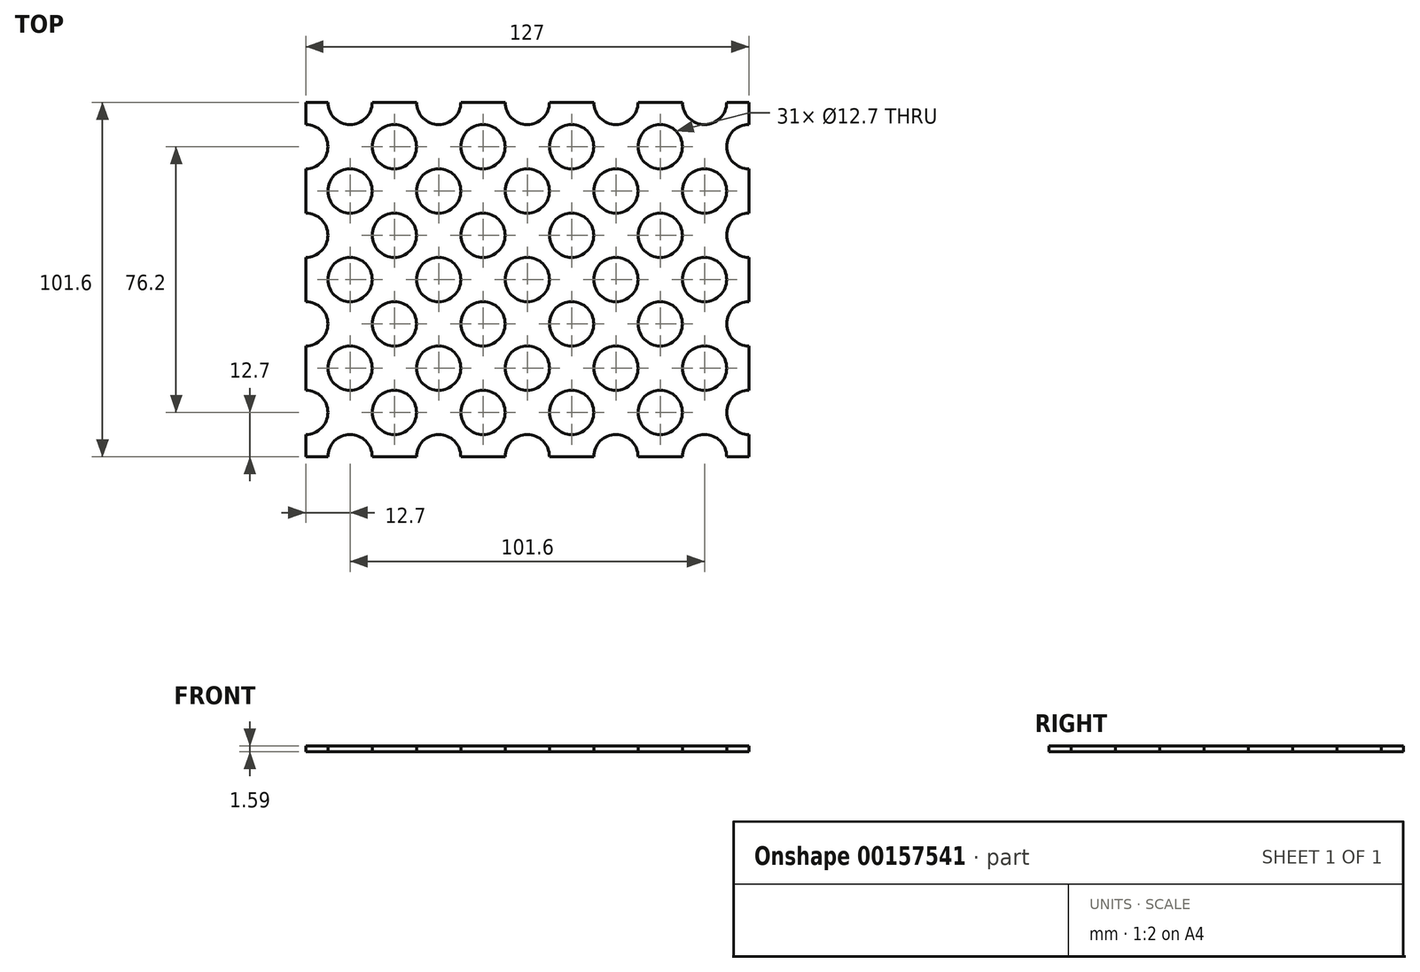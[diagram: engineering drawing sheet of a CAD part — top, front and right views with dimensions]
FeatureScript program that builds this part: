
annotation { "Feature Type Name" : "Feature", "Feature Type Description" : "" }
export const myFeature = defineFeature(function(context is Context, id is Id, definition is map)
    precondition{}
    {
        {
            var Q0;
            Q0=qCreatedBy(makeId("Top.planeOp"),FACE);
            var sketch = newSketch(context, id + "F0", { "sketchPlane" : qUnion([Q0])});
            skLineSegment(sketch, "E0.bottom", {"start": v(-63.5, -50.8) * mm, "end": v(63.5, -50.8) * mm});
            skLineSegment(sketch, "E0.top", {"start": v(-63.5, 50.8) * mm, "end": v(63.5, 50.8) * mm});
            skLineSegment(sketch, "E0.left", {"start": v(-63.5, -50.8) * mm, "end": v(-63.5, 50.8) * mm});
            skLineSegment(sketch, "E0.right", {"start": v(63.5, -50.8) * mm, "end": v(63.5, 50.8) * mm});
            skCircle(sketch, "E1", {"center": v(-63.5, 38.1) * mm, "radius": 6.35 * mm});
            skCircle(sketch, "E2.0.1.0", {"center": v(-63.5, 12.7) * mm, "radius": 6.35 * mm});
            skCircle(sketch, "E2.0.2.0", {"center": v(-63.5, -12.7) * mm, "radius": 6.35 * mm});
            skCircle(sketch, "E2.1.0.0", {"center": v(-38.1, 38.1) * mm, "radius": 6.35 * mm});
            skCircle(sketch, "E2.1.1.0", {"center": v(-38.1, 12.7) * mm, "radius": 6.35 * mm});
            skCircle(sketch, "E2.1.2.0", {"center": v(-38.1, -12.7) * mm, "radius": 6.35 * mm});
            skCircle(sketch, "E2.2.0.0", {"center": v(-12.7, 38.1) * mm, "radius": 6.35 * mm});
            skCircle(sketch, "E2.2.1.0", {"center": v(-12.7, 12.7) * mm, "radius": 6.35 * mm});
            skCircle(sketch, "E2.2.2.0", {"center": v(-12.7, -12.7) * mm, "radius": 6.35 * mm});
            skCircle(sketch, "E2.3.0.0", {"center": v(12.7, 38.1) * mm, "radius": 6.35 * mm});
            skCircle(sketch, "E2.3.1.0", {"center": v(12.7, 12.7) * mm, "radius": 6.35 * mm});
            skCircle(sketch, "E2.3.2.0", {"center": v(12.7, -12.7) * mm, "radius": 6.35 * mm});
            skCircle(sketch, "E2.4.0.0", {"center": v(38.1, 38.1) * mm, "radius": 6.35 * mm});
            skCircle(sketch, "E2.4.1.0", {"center": v(38.1, 12.7) * mm, "radius": 6.35 * mm});
            skCircle(sketch, "E2.4.2.0", {"center": v(38.1, -12.7) * mm, "radius": 6.35 * mm});
            skCircle(sketch, "E2.5.0.0", {"center": v(63.5, 38.1) * mm, "radius": 6.35 * mm});
            skCircle(sketch, "E2.5.1.0", {"center": v(63.5, 12.7) * mm, "radius": 6.35 * mm});
            skCircle(sketch, "E2.5.2.0", {"center": v(63.5, -12.7) * mm, "radius": 6.35 * mm});
            skLineSegment(sketch, "E2.direction1", {"start": v(-63.5, 38.1) * mm, "end": v(-38.1, 38.1) * mm, "construction": true});
            skLineSegment(sketch, "E2.direction2", {"start": v(-63.5, 38.1) * mm, "end": v(-63.5, 12.7) * mm, "construction": true});
            skCircle(sketch, "E3", {"center": v(-50.8, 25.4) * mm, "radius": 6.35 * mm});
            skPoint(sketch, "E3.centerSnap0", {"position": v(-63.5, 25.4) * mm});
            skCircle(sketch, "E4.0.0.3", {"center": v(-63.5, -38.1) * mm, "radius": 6.35 * mm});
            skCircle(sketch, "E4.0.1.3", {"center": v(-38.1, -38.1) * mm, "radius": 6.35 * mm});
            skCircle(sketch, "E4.0.2.3", {"center": v(-12.7, -38.1) * mm, "radius": 6.35 * mm});
            skCircle(sketch, "E4.0.3.3", {"center": v(12.7, -38.1) * mm, "radius": 6.35 * mm});
            skCircle(sketch, "E4.0.4.3", {"center": v(38.1, -38.1) * mm, "radius": 6.35 * mm});
            skCircle(sketch, "E4.0.5.3", {"center": v(63.5, -38.1) * mm, "radius": 6.35 * mm});
            skCircle(sketch, "E5.0.1.0", {"center": v(-50.8, 0) * mm, "radius": 6.35 * mm});
            skCircle(sketch, "E5.0.2.0", {"center": v(-50.8, -25.4) * mm, "radius": 6.35 * mm});
            skCircle(sketch, "E5.0.3.0", {"center": v(-50.8, -50.8) * mm, "radius": 6.35 * mm});
            skCircle(sketch, "E5.1.0.0", {"center": v(-25.4, 25.4) * mm, "radius": 6.35 * mm});
            skCircle(sketch, "E5.1.1.0", {"center": v(-25.4, 0) * mm, "radius": 6.35 * mm});
            skCircle(sketch, "E5.1.2.0", {"center": v(-25.4, -25.4) * mm, "radius": 6.35 * mm});
            skCircle(sketch, "E5.1.3.0", {"center": v(-25.4, -50.8) * mm, "radius": 6.35 * mm});
            skCircle(sketch, "E5.2.0.0", {"center": v(0, 25.4) * mm, "radius": 6.35 * mm});
            skCircle(sketch, "E5.2.1.0", {"center": v(0, 0) * mm, "radius": 6.35 * mm});
            skCircle(sketch, "E5.2.2.0", {"center": v(0, -25.4) * mm, "radius": 6.35 * mm});
            skCircle(sketch, "E5.2.3.0", {"center": v(0, -50.8) * mm, "radius": 6.35 * mm});
            skCircle(sketch, "E5.3.0.0", {"center": v(25.4, 25.4) * mm, "radius": 6.35 * mm});
            skCircle(sketch, "E5.3.1.0", {"center": v(25.4, 0) * mm, "radius": 6.35 * mm});
            skCircle(sketch, "E5.3.2.0", {"center": v(25.4, -25.4) * mm, "radius": 6.35 * mm});
            skCircle(sketch, "E5.3.3.0", {"center": v(25.4, -50.8) * mm, "radius": 6.35 * mm});
            skCircle(sketch, "E5.4.0.0", {"center": v(50.8, 25.4) * mm, "radius": 6.35 * mm});
            skCircle(sketch, "E5.4.1.0", {"center": v(50.8, 0) * mm, "radius": 6.35 * mm});
            skCircle(sketch, "E5.4.2.0", {"center": v(50.8, -25.4) * mm, "radius": 6.35 * mm});
            skCircle(sketch, "E5.4.3.0", {"center": v(50.8, -50.8) * mm, "radius": 6.35 * mm});
            skLineSegment(sketch, "E5.direction1", {"start": v(-50.8, 25.4) * mm, "end": v(-25.4, 25.4) * mm, "construction": true});
            skLineSegment(sketch, "E5.direction2", {"start": v(-50.8, 25.4) * mm, "end": v(-50.8, 0) * mm, "construction": true});
            skLineSegment(sketch, "E6", {"start": v(-63.5, 38.1) * mm, "end": v(63.5, 38.1) * mm, "construction": true});
            skCircle(sketch, "E7.MirrorC", {"center": v(25.4, 50.8) * mm, "radius": 6.35 * mm});
            skCircle(sketch, "E8.MirrorC", {"center": v(50.8, 50.8) * mm, "radius": 6.35 * mm});
            skCircle(sketch, "E9.MirrorC", {"center": v(0, 50.8) * mm, "radius": 6.35 * mm});
            skCircle(sketch, "E10.MirrorC", {"center": v(-25.4, 50.8) * mm, "radius": 6.35 * mm});
            skCircle(sketch, "E11.MirrorC", {"center": v(-50.8, 50.8) * mm, "radius": 6.35 * mm});
            skSolve(sketch);
        }
        {
            var Q0;
            {var subQ24=sQuery(id+"F0.wireOp",EDGE,"E0.top");Q0=makeQuery(id+"F0.imprint","IMPRINT",FACE,{"disambiguationData":[TD([[makeQuery(id+"F0.imprint","IMPRINT",EDGE,{"derivedFrom":subQ24}),-1.0]])]});}
            extrude(context, id + "F1", {"entities" : qUnion([Q0]), "depth" : 1.59 * mm});
        }
    });
